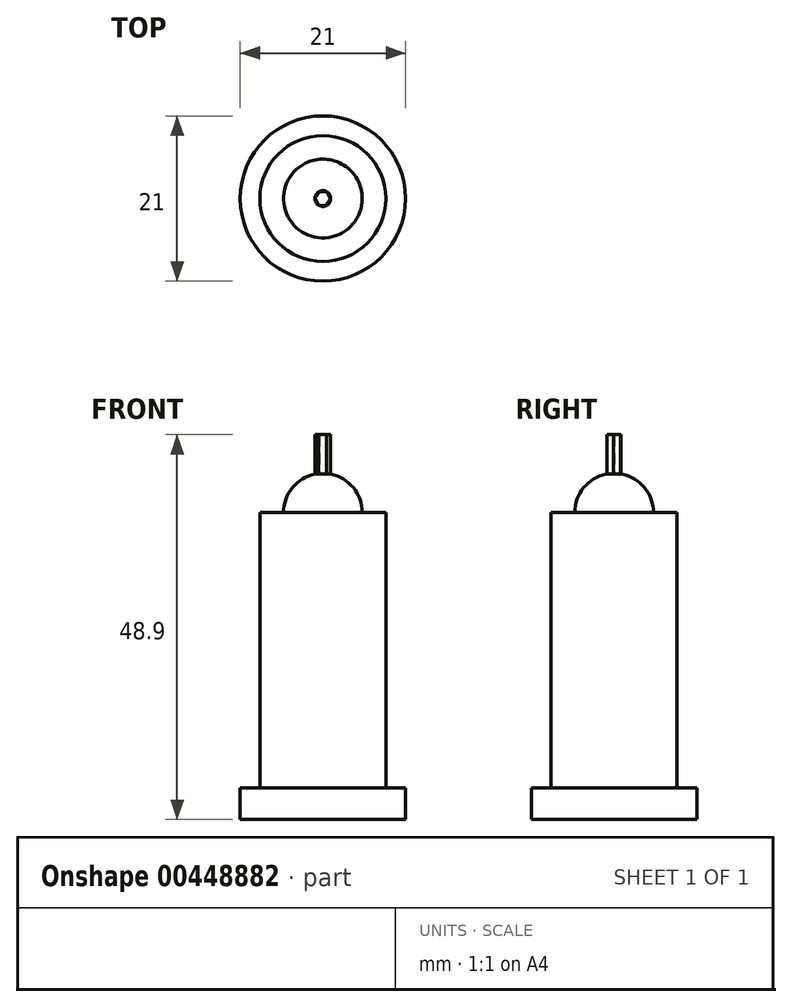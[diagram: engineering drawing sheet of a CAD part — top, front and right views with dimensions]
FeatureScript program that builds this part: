
annotation { "Feature Type Name" : "Feature", "Feature Type Description" : "" }
export const myFeature = defineFeature(function(context is Context, id is Id, definition is map)
    precondition{}
    {
        {
            var Q0;
            Q0=qCreatedBy(makeId("Top.planeOp"),FACE);
            var sketch = newSketch(context, id + "F0", { "sketchPlane" : qUnion([Q0])});
            skCircle(sketch, "E0", {"center": v(0, 0) * mm, "radius": 10.5 * mm});
            skSolve(sketch);
        }
        {
            var Q0;
            Q0=qSketchRegion(id+"F0",true);
            extrude(context, id + "F1", {"entities" : qUnion([Q0]), "depth" : 4 * mm});
        }
        {
            var Q0;
            Q0=qCreatedBy(makeId("Top.planeOp"),FACE);
            var sketch = newSketch(context, id + "F2", { "sketchPlane" : qUnion([Q0])});
            skCircle(sketch, "E1", {"center": v(0, 0) * mm, "radius": 8 * mm});
            skSolve(sketch);
        }
        {
            var Q0;
            Q0=qSketchRegion(id+"F2",true);
            extrude(context, id + "F3", {"entities" : qUnion([Q0]), "operationType" : NewBodyOperationType.ADD, "depth" : 39 * mm});
        }
        {
            var Q0;
            Q0=qCreatedBy(makeId("Right.planeOp"),FACE);
            var sketch = newSketch(context, id + "F4", { "sketchPlane" : qUnion([Q0])});
            skLineSegment(sketch, "E2", {"start": v(0, 44) * mm, "end": v(0, 39) * mm});
            skLineSegment(sketch, "E3", {"start": v(0, 39) * mm, "end": v(5, 39) * mm});
            skArc(sketch, "E4", {"start": v(5, 39) * mm, "mid": v(3.54, 42.54) * mm, "end": v(0, 44) * mm});
            skLineSegment(sketch, "E5", {"start": v(0, 43.9) * mm, "end": v(1, 43.9) * mm});
            skSolve(sketch);
        }
        {
            var Q0;
            {var subQ0=sQuery(id+"F4.wireOp",EDGE,"E3");Q0=makeQuery(id+"F4.imprint","IMPRINT",FACE,{"disambiguationData":[TD([[makeQuery(id+"F4.imprint","IMPRINT",EDGE,{"derivedFrom":subQ0}),1.0]])]});}
            var Q1;
            Q1=sQuery(id+"F4.wireOp",EDGE,"E2");
            revolve(context, id + "F5", {"operationType" : NewBodyOperationType.ADD, "entities" : qUnion([Q0]), "axis" : qUnion([Q1]), "revolveType" : RevolveType.FULL});
        }
        {
            var Q0;
            Q0=makeQuery(id+"F5.opRevolve","SWEPT_FACE",FACE,{"disambiguationData":[OSD([sQuery(id+"F4.wireOp",EDGE,"E5")])]});
            var sketch = newSketch(context, id + "F6", { "sketchPlane" : qUnion([Q0])});
            skCircle(sketch, "E6.cCircle", {"center": v(0, 0) * mm, "radius": 0.87 * mm, "construction": true});
            skLineSegment(sketch, "E6.0", {"start": v(1, -0.07) * mm, "end": v(0.44, -0.9) * mm});
            skLineSegment(sketch, "E6.1", {"start": v(0.44, -0.9) * mm, "end": v(-0.56, -0.83) * mm});
            skLineSegment(sketch, "E6.2", {"start": v(-0.56, -0.83) * mm, "end": v(-1, 0.07) * mm});
            skLineSegment(sketch, "E6.3", {"start": v(-1, 0.07) * mm, "end": v(-0.44, 0.9) * mm});
            skLineSegment(sketch, "E6.4", {"start": v(-0.44, 0.9) * mm, "end": v(0.56, 0.83) * mm});
            skLineSegment(sketch, "E6.5", {"start": v(0.56, 0.83) * mm, "end": v(1, -0.07) * mm});
            skPoint(sketch, "E6.0.midPoint", {"position": v(0.72, -0.48) * mm});
            skSolve(sketch);
        }
        {
            var Q0;
            Q0 = qSketchRegion(id + "F6", true);
            extrude(context, id + "F7", {"entities" : qUnion([Q0]), "operationType" : NewBodyOperationType.ADD, "depth" : 5 * mm});
        }
    });
